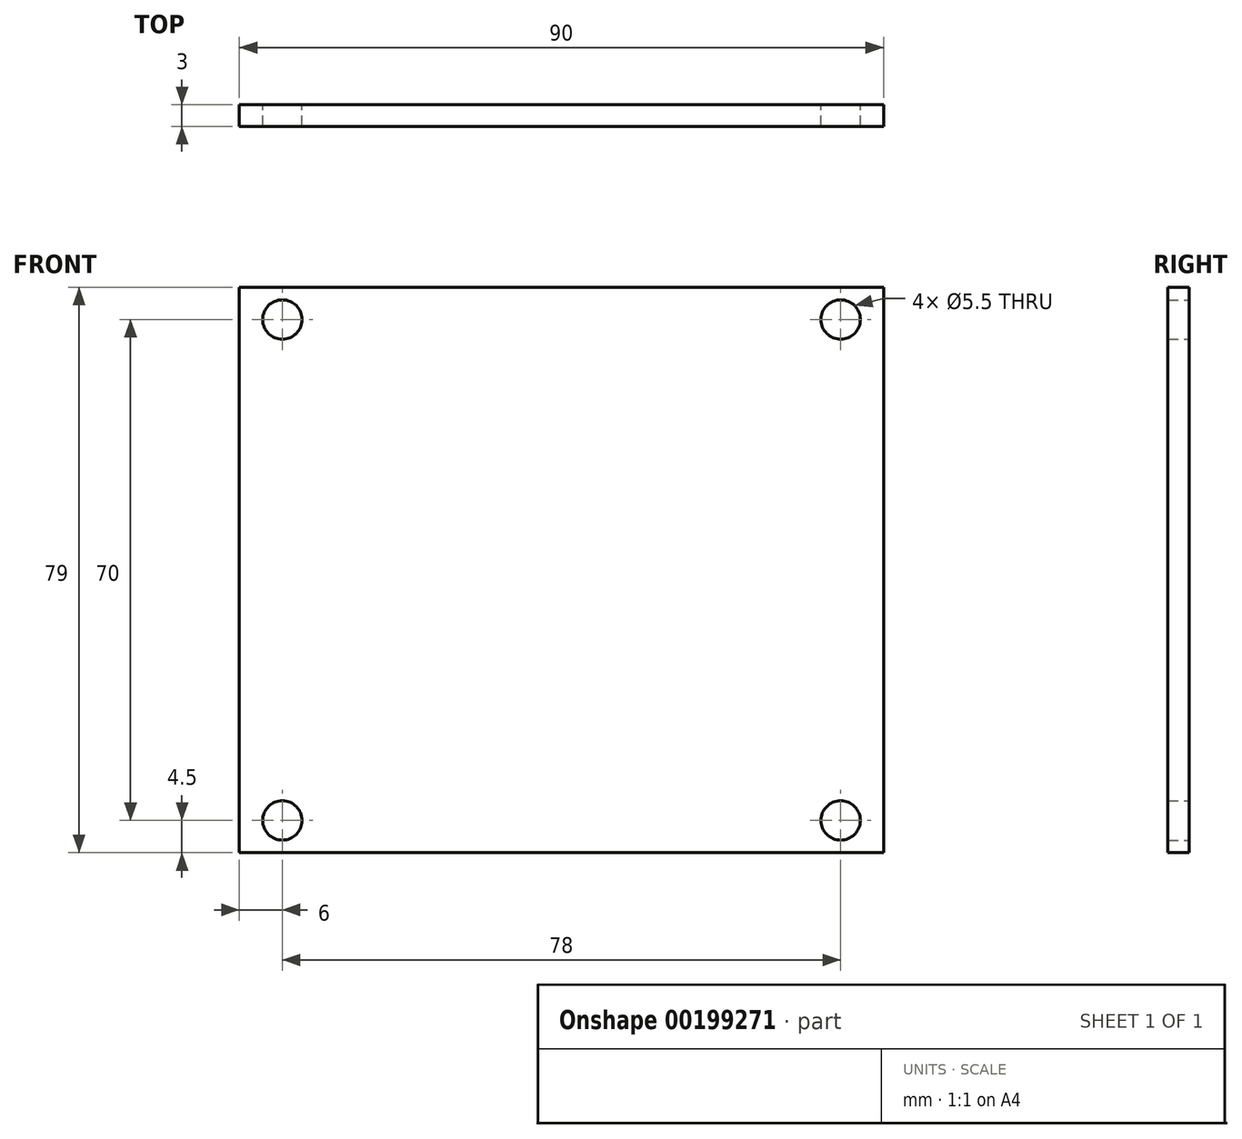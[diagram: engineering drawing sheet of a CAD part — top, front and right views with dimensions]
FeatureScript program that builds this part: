
annotation { "Feature Type Name" : "Feature", "Feature Type Description" : "" }
export const myFeature = defineFeature(function(context is Context, id is Id, definition is map)
    precondition{}
    {
        {
            var Q0;
            Q0=qCreatedBy(makeId("Front.planeOp"),FACE);
            var sketch = newSketch(context, id + "F0", { "sketchPlane" : qUnion([Q0])});
            skLineSegment(sketch, "E0.bottom", {"start": v(-45, 39.5) * mm, "end": v(45, 39.5) * mm});
            skLineSegment(sketch, "E0.top", {"start": v(-45, -39.5) * mm, "end": v(45, -39.5) * mm});
            skLineSegment(sketch, "E0.left", {"start": v(-45, 39.5) * mm, "end": v(-45, -39.5) * mm});
            skLineSegment(sketch, "E0.right", {"start": v(45, 39.5) * mm, "end": v(45, -39.5) * mm});
            skPoint(sketch, "E0.middle", {"position": v(0, 0) * mm});
            skLineSegment(sketch, "E1", {"start": v(0, 39.5) * mm, "end": v(0, -39.5) * mm, "construction": true});
            skLineSegment(sketch, "E2", {"start": v(-45, 0) * mm, "end": v(45, 0) * mm, "construction": true});
            skCircle(sketch, "E3", {"center": v(-39, 35) * mm, "radius": 2.75 * mm});
            skCircle(sketch, "E4.MirrorC", {"center": v(39, 35) * mm, "radius": 2.75 * mm});
            skCircle(sketch, "E5.MirrorC", {"center": v(-39, -35) * mm, "radius": 2.75 * mm});
            skCircle(sketch, "E6.MirrorC", {"center": v(39, -35) * mm, "radius": 2.75 * mm});
            skSolve(sketch);
        }
        {
            var Q0;
            Q0 = qSketchRegion(id + "F0", true);
            extrude(context, id + "F1", {"entities" : qUnion([Q0]), "depth" : 3 * mm});
        }
    });
